# Revit family: BUILDMAT-POPCONPN-32mm_Concrete_Pop_Up_Waste-Champagne_Pink
name_source: partatom
category: Plumbing Fixtures
units: mm (PartAtom-declared; Revit-internal decimal feet)

## family parameters
Always vertical = Yes
Cut with Voids When Loaded = Yes
Enable Cutting in Views = Yes
Maintain Annotation Orientation = No
Part Type = Normal
Room Calculation Point = No
Round Connector Dimension = Use Diameter
Shared = No
Work Plane-Based = Yes

## types (1)
- BUILDMAT-POPCONPN-32mm_Concrete_Pop_Up_Waste-Champagne_Pink
    Default Elevation = 1219 mm
    Depth = 66 mm  [stored 0.216535 ft]
    Lock_Material = BUILDMAT Brass Gold
    MainBody_Material = BUILDMAT Stainless Steel
    PopUp_Material = BUILDMAT Champage Pink
    Width = 66 mm  [stored 0.216535 ft]

note: [stored X ft] marks values corroborated as IEEE doubles in the binary element streams (Revit-internal decimal feet)

## geometry (parser evidence)
native form markers: Sweep x1
no freeform markers — native parametric forms only
